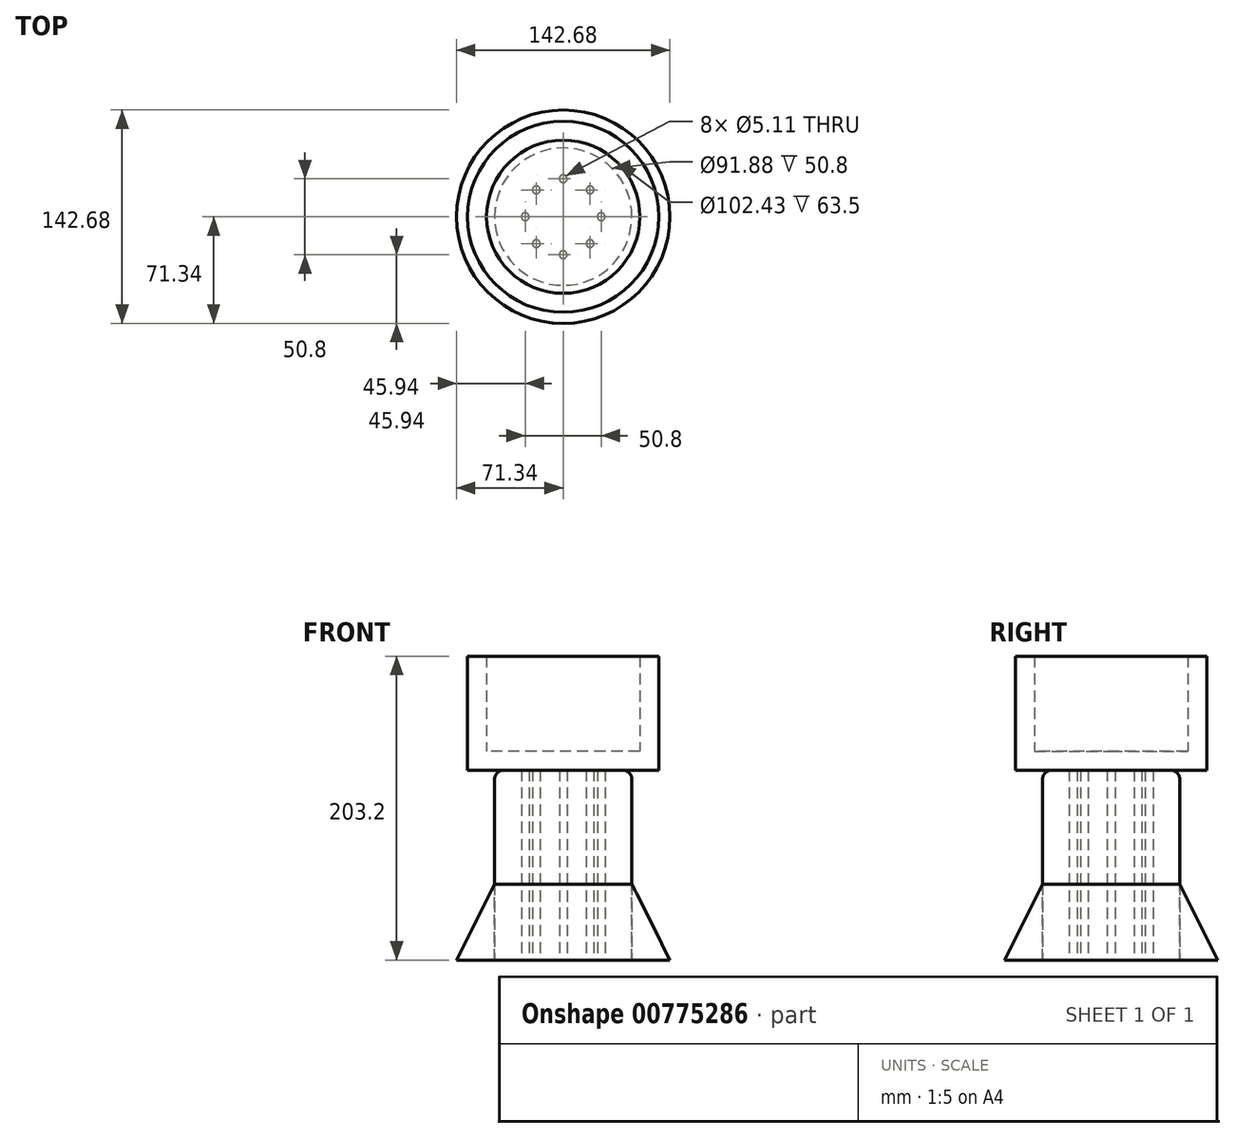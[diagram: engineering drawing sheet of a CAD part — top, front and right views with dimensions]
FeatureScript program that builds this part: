
annotation { "Feature Type Name" : "Feature", "Feature Type Description" : "" }
export const myFeature = defineFeature(function(context is Context, id is Id, definition is map)
    precondition{}
    {
        {
            var Q0;
            Q0=qCreatedBy(makeId("Top.planeOp"),FACE);
            var sketch = newSketch(context, id + "F0", { "sketchPlane" : qUnion([Q0])});
            skCircle(sketch, "E0", {"center": v(0, 0) * mm, "radius": 45.94 * mm});
            skSolve(sketch);
        }
        {
            var Q0;
            Q0=makeQuery(id+"F0.imprint","IMPRINT",FACE,{"disambiguationData":[TD([[makeQuery(id+"F0.imprint","IMPRINT",EDGE,{"derivedFrom":sQuery(id+"F0.wireOp",EDGE,"E0")}),1.0]])]});
            var Q1;
            Q1=sQuery(id+"F0.wireOp",EDGE,"E0");
            extrude(context, id + "F1", {"entities" : qUnion([Q0]), "surfaceEntities" : qUnion([Q1]), "depth" : 127 * mm, "offsetDistance" : 25.4 * mm});
        }
        {
            var Q0;
            Q0=makeQuery(id+"F1.opExtrude","CAP_FACE",FACE,{"disambiguationData":[OSD([sQuery(id+"F0.wireOp",EDGE,"E0")])],"isStart":false});
            var sketch = newSketch(context, id + "F2", { "sketchPlane" : qUnion([Q0])});
            skCircle(sketch, "E1", {"center": v(0, 0) * mm, "radius": 63.91 * mm});
            skSolve(sketch);
        }
        {
            var Q0;
            Q0=makeQuery(id+"F2.imprint","IMPRINT",FACE,{"disambiguationData":[TD([[makeQuery(id+"F2.imprint","IMPRINT",EDGE,{"derivedFrom":sQuery(id+"F2.wireOp",EDGE,"E1")}),1.0]])]});
            var Q1;
            Q1=makeQuery(id+"F2.imprint","IMPRINT",FACE,{"disambiguationData":[TD([[makeQuery(id+"F2.imprint","IMPRINT",EDGE,{"derivedFrom":makeQuery(id+"F1.opExtrude","CAP_EDGE",EDGE,{"disambiguationData":[OSD([sQuery(id+"F0.wireOp",EDGE,"E0")])],"isStart":false})}),1.0]])]});
            extrude(context, id + "F3", {"entities" : qUnion([Q0, Q1]), "depth" : 76.2 * mm, "offsetDistance" : 25.4 * mm});
        }
        {
            var Q0;
            Q0=makeQuery(id+"F1.opExtrude","CAP_EDGE",EDGE,{"disambiguationData":[OSD([sQuery(id+"F0.wireOp",EDGE,"E0")])],"isStart":false});
            fillet(context, id + "F4", {"entities" : qUnion([Q0]), "radius" : 6.35 * mm, "tangentPropagation" : true, "allowEdgeOverflow" : false});
        }
        {
            var Q0;
            Q0=makeQuery(id+"F3.opExtrude","CAP_FACE",FACE,{"disambiguationData":[OSD([sQuery(id+"F2.wireOp",EDGE,"E1")])],"isStart":false});
            shell(context, id + "F5", {"entities" : qUnion([Q0]), "thickness" : 12.7 * mm});
        }
        {
            var Q0;
            Q0=makeQuery(id+"F1.opExtrude","CAP_FACE",FACE,{"disambiguationData":[OSD([sQuery(id+"F0.wireOp",EDGE,"E0")])],"isStart":true});
            var sketch = newSketch(context, id + "F6", { "sketchPlane" : qUnion([Q0])});
            skPoint(sketch, "E2", {"position": v(0, 0) * mm});
            skPoint(sketch, "E3", {"position": v(0, -25.4) * mm});
            skPoint(sketch, "E4.1.0", {"position": v(17.96, -17.96) * mm});
            skPoint(sketch, "E4.2.0", {"position": v(25.4, 0) * mm});
            skPoint(sketch, "E5.0.3.0", {"position": v(17.96, 17.96) * mm});
            skPoint(sketch, "E5.0.4.0", {"position": v(0, 25.4) * mm});
            skPoint(sketch, "E5.0.5.0", {"position": v(-17.96, 17.96) * mm});
            skPoint(sketch, "E5.0.6.0", {"position": v(-25.4, 0) * mm});
            skPoint(sketch, "E5.0.7.0", {"position": v(-17.96, -17.96) * mm});
            skSolve(sketch);
        }
        {
            var Q0;
            Q0=sQuery(id+"F6.wireOp",VERTEX,"E3");
            var Q1;
            Q1=sQuery(id+"F6.wireOp",VERTEX,"E5.0.7.0");
            var Q2;
            Q2=sQuery(id+"F6.wireOp",VERTEX,"E5.0.6.0");
            var Q3;
            Q3=sQuery(id+"F6.wireOp",VERTEX,"E5.0.4.0");
            var Q4;
            Q4=sQuery(id+"F6.wireOp",VERTEX,"E5.0.3.0");
            var Q5;
            Q5=sQuery(id+"F6.wireOp",VERTEX,"E4.2.0");
            var Q6;
            Q6=sQuery(id+"F6.wireOp",VERTEX,"E4.1.0");
            var Q7;
            Q7=sQuery(id+"F6.wireOp",VERTEX,"E5.0.5.0");
            var Q8;
            Q8=makeQuery(id+"F1.opExtrude","SWEPT_BODY",BODY,{"disambiguationData":[OSD([sQuery(id+"F0.wireOp",EDGE,"E0")])]});
            hole(context, id + "F7", {"style" : HoleStyle.SIMPLE, "endStyle" : HoleEndStyle.THROUGH, "standardTappedOrClearance" : lookupTablePath({ "fit" : "Close (ASME)", "standard" : "ANSI", "engagement" : "75%", "pitch" : "20 tpi", "size" : "1/4", "type" : "Tapped" }), "standardBlindInLast" : lookupTablePath({ "fit" : "Close", "standard" : "ANSI", "engagement" : "75%", "pitch" : "20 tpi", "size" : "1/4", "type" : "Tapped" }), "holeDiameter" : 5.1 * mm, "majorDiameter" : 6.35 * mm, "showTappedDepth" : true, "isTappedThrough" : true, "tappedDepth" : 12.7 * mm, "tapClearance" : 3, "locations" : qUnion([Q0, Q1, Q2, Q3, Q4, Q5, Q6, Q7]), "scope" : qUnion([Q8])});
        }
        {
            var Q0;
            Q0=qCreatedBy(makeId("Front.planeOp"),FACE);
            var sketch = newSketch(context, id + "F8", { "sketchPlane" : qUnion([Q0])});
            skLineSegment(sketch, "E6", {"start": v(45.94, 0) * mm, "end": v(45.94, 50.8) * mm});
            skLineSegment(sketch, "E7", {"start": v(45.94, 0) * mm, "end": v(71.34, 0) * mm});
            skLineSegment(sketch, "E8", {"start": v(71.34, 0) * mm, "end": v(45.94, 50.8) * mm});
            skSolve(sketch);
        }
        {
            var Q0;
            Q0=makeQuery(id+"F8.imprint","IMPRINT",FACE,{"disambiguationData":[TD([[makeQuery(id+"F8.imprint","IMPRINT",EDGE,{"derivedFrom":sQuery(id+"F8.wireOp",EDGE,"E6")}),-1.0]])]});
            var Q1;
            Q1=makeQuery(id+"F3.opExtrude","SWEPT_FACE",FACE,{"disambiguationData":[OSD([sQuery(id+"F2.wireOp",EDGE,"E1")])]});
            revolve(context, id + "F9", {"operationType" : NewBodyOperationType.ADD, "surfaceOperationType" : NewSurfaceOperationType.NEW, "entities" : qUnion([Q0]), "axis" : qUnion([Q1]), "revolveType" : RevolveType.FULL});
        }
    });
